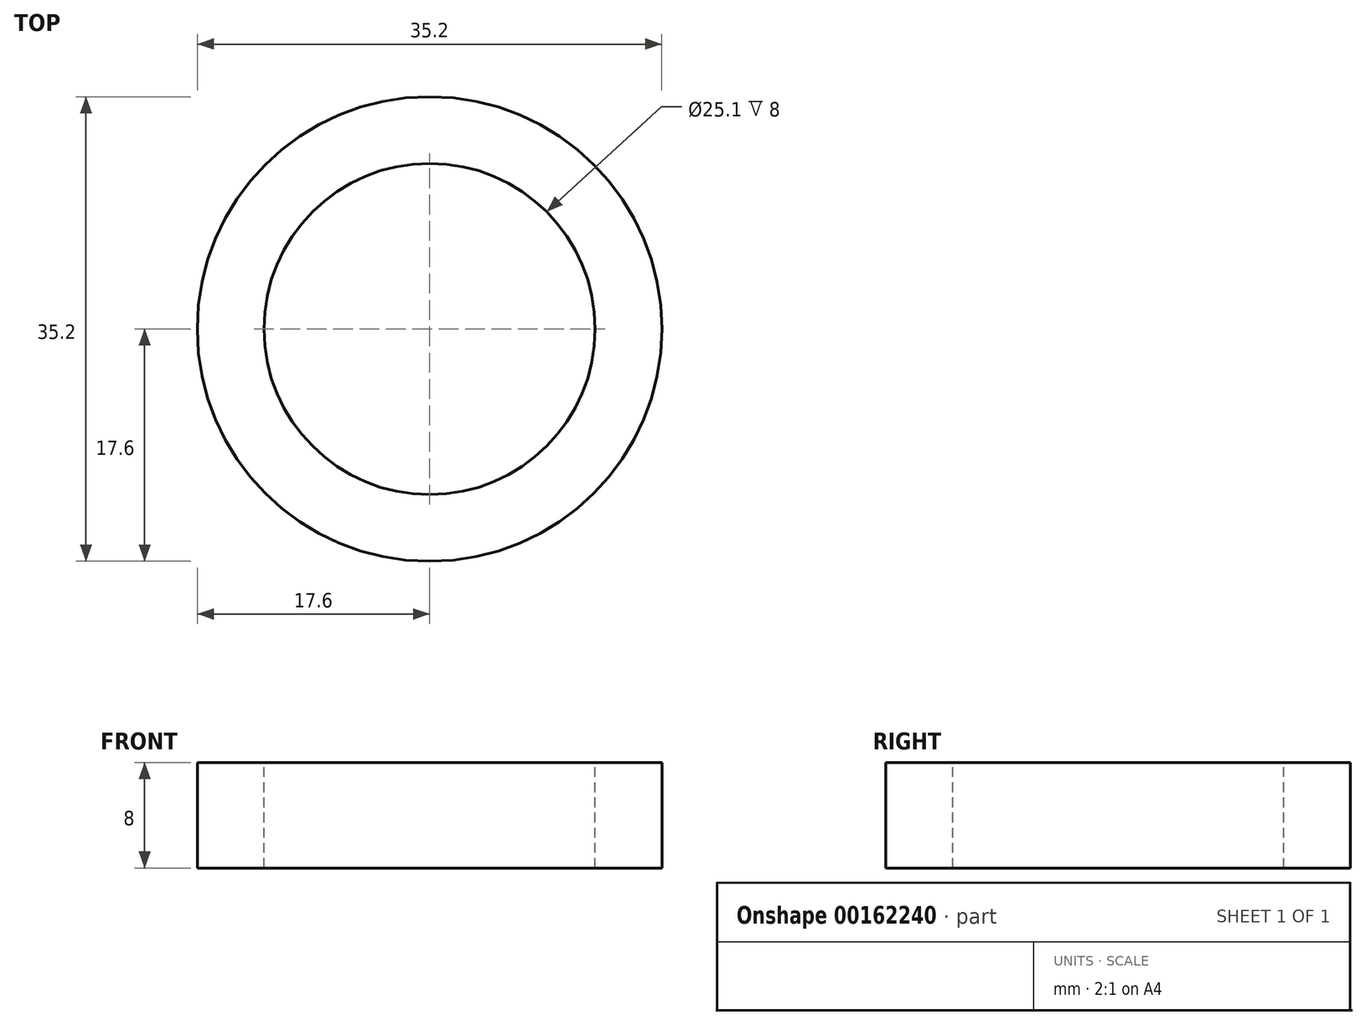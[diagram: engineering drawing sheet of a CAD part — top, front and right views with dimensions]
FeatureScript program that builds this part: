
annotation { "Feature Type Name" : "Feature", "Feature Type Description" : "" }
export const myFeature = defineFeature(function(context is Context, id is Id, definition is map)
    precondition{}
    {
        {
            var Q0;
            Q0=qCreatedBy(makeId("Top.planeOp"),FACE);
            var sketch = newSketch(context, id + "F0", { "sketchPlane" : qUnion([Q0])});
            skCircle(sketch, "E0", {"center": v(0, 0) * mm, "radius": 17.6 * mm});
            skPoint(sketch, "E0.first.point", {"position": v(6.15, 16.5) * mm});
            skPoint(sketch, "E0.second.point", {"position": v(0, -17.6) * mm});
            skSolve(sketch);
        }
        {
            var Q0;
            Q0=makeQuery(id+"F0.imprint","IMPRINT",FACE,{"disambiguationData":[TD([[makeQuery(id+"F0.imprint","IMPRINT",EDGE,{"derivedFrom":sQuery(id+"F0.wireOp",EDGE,"E0")}),1.0]])]});
            extrude(context, id + "F1", {"entities" : qUnion([Q0]), "depth" : 8 * mm});
        }
        {
            var Q0;
            Q0=makeQuery(id+"F1.opExtrude","CAP_FACE",FACE,{"disambiguationData":[OSD([sQuery(id+"F0.wireOp",EDGE,"E0")])],"isStart":false});
            var sketch = newSketch(context, id + "F2", { "sketchPlane" : qUnion([Q0])});
            skCircle(sketch, "E1", {"center": v(0, 0) * mm, "radius": 12.55 * mm});
            skSolve(sketch);
        }
        {
            var Q0;
            Q0 = qSketchRegion(id + "F2", true);
            extrude(context, id + "F3", {"entities" : qUnion([Q0]), "operationType" : NewBodyOperationType.REMOVE, "oppositeDirection" : true, "depth" : 9 * mm});
        }
    });
